# Revit family: Basin-Countertop-Pedestal-American_Standard-Tropic_Petite-0403_Series
name_source: partatom
category: Plumbing Fixtures
revit_build: Autodesk Revit 2014 (Build: 20130308_1515(x64)
units: mm (PartAtom-declared; Revit-internal decimal feet)

## types (4) — shared parameters
Assembly Code = D2010310
Basin Shape = Semi Circle
CW Connection = Yes
CWFU = 1.5
Cold Water Connection Diameter = 1/2"
Cold Water Connection Height = 23 7/8"
Cold Water Connection Radius = 1/4"
Cold Water Connection Width = 4"
Default Elevation = 34"
Description = Tropic Petite Countertop Sink.
HW Connection = Yes
HWFU = 1.5
Hot Water Connection Diameter = 1"
Hot Water Connection Height = 23 7/8"
Hot Water Connection Radius = 1/4"
Hot Water Connection Width = 4"
Installation Type = Wall Mounted
Manufacturer = American Standard
Material = Vitreous China-American Standard-020-White
Price = Prices may vary. Please consult Manufacturer Representative for most up-to-date price list.
Product Documentation Link = https://www.americanstandard-us.com
Product Page URL = https://www.americanstandard-us.com
Revised Date = 01/19/2017
URL = http://www.americanstandard-us.com
Vent Connection = No
WFU = 2
Waste Connection = Yes
Waste Connection Diameter = 1 1/4"
Waste Connection Height = 22"
Waste Connection Radius = 5/8"

## per-type parameters (varying)
| type | Hole Punch Location | Model | Pedestal Option |
| 0403.008 | 8" | 0403.008 | No |
| 0403.004 | 4" | 0403.004 | No |
| 0403.400 | 4" | 0403.400 | Yes |
| 0403.800 | 8" | 0403.400 | Yes |

## geometry (parser evidence)
native form markers: Sweep x1
no freeform markers — native parametric forms only
